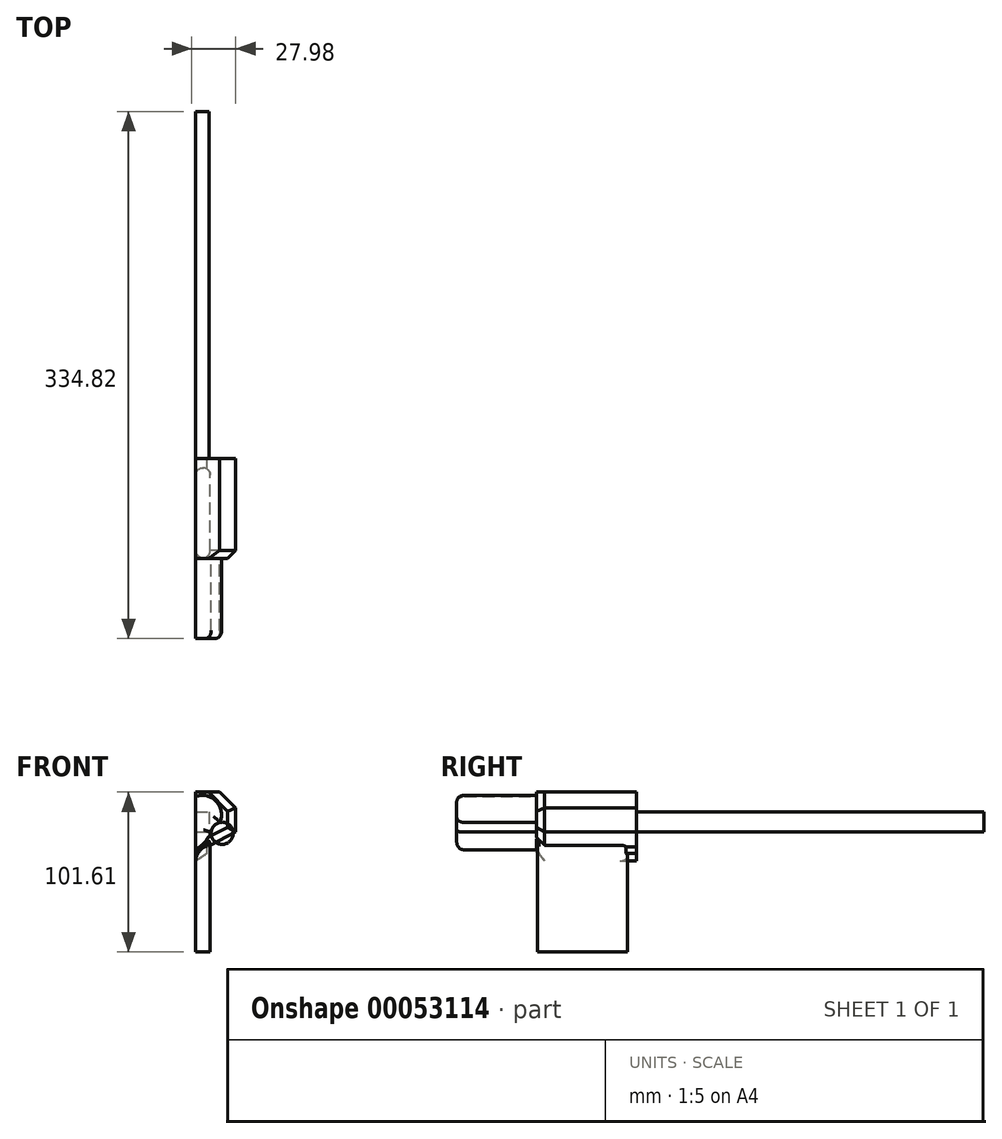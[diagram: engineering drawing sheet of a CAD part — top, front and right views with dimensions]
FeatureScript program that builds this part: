
annotation { "Feature Type Name" : "Feature", "Feature Type Description" : "" }
export const myFeature = defineFeature(function(context is Context, id is Id, definition is map)
    precondition{}
    {
        {
            var Q0;
            Q0=qCreatedBy(makeId("Top.planeOp"),FACE);
            var sketch = newSketch(context, id + "F0", { "sketchPlane" : qUnion([Q0])});
            skLineSegment(sketch, "E0.bottom", {"start": v(0, -78.27) * mm, "end": v(8.58, -78.27) * mm});
            skLineSegment(sketch, "E0.top", {"start": v(0, 142.25) * mm, "end": v(8.58, 142.25) * mm});
            skLineSegment(sketch, "E0.left", {"start": v(0, -78.27) * mm, "end": v(0, 142.25) * mm});
            skLineSegment(sketch, "E0.right", {"start": v(8.58, -78.27) * mm, "end": v(8.58, 142.25) * mm});
            skSolve(sketch);
        }
        {
            var Q0;
            Q0=makeQuery(id+"F0.imprint","IMPRINT",FACE,{"disambiguationData":[TD([[makeQuery(id+"F0.imprint","IMPRINT",EDGE,{"derivedFrom":sQuery(id+"F0.wireOp",EDGE,"E0.bottom")}),1.0]])]});
            extrude(context, id + "F1", {"entities" : qUnion([Q0]), "depth" : 12.7 * mm});
        }
        {
            var Q0;
            Q0=makeQuery(id+"F1.opExtrude","SWEPT_FACE",FACE,{"disambiguationData":[OSD([sQuery(id+"F0.wireOp",EDGE,"E0.bottom")])]});
            var sketch = newSketch(context, id + "F2", { "sketchPlane" : qUnion([Q0])});
            skLineSegment(sketch, "E1.bottom", {"start": v(0, 25.4) * mm, "end": v(25.38, 25.4) * mm});
            skLineSegment(sketch, "E1.left", {"start": v(0, 25.4) * mm, "end": v(0, 0) * mm});
            skLineSegment(sketch, "E1.right", {"start": v(25.38, 25.4) * mm, "end": v(25.38, 0) * mm});
            skLineSegment(sketch, "E2", {"start": v(25.38, 0) * mm, "end": v(7.29, -9.27) * mm});
            skLineSegment(sketch, "E3", {"start": v(7.29, -9.27) * mm, "end": v(7.29, -13.57) * mm});
            skLineSegment(sketch, "E4", {"start": v(7.29, -13.57) * mm, "end": v(0, -18.36) * mm});
            skLineSegment(sketch, "E5", {"start": v(0, -18.36) * mm, "end": v(0, 0) * mm});
            skSolve(sketch);
        }
        {
            var Q0;
            Q0 = qSketchRegion(id + "F2", true);
            extrude(context, id + "F3", {"entities" : qUnion([Q0]), "operationType" : NewBodyOperationType.ADD, "depth" : 63.5 * mm});
        }
        {
            var Q0;
            Q0=makeQuery(id+"F3.opExtrude","CAP_FACE",FACE,{"disambiguationData":[OSD([sQuery(id+"F2.wireOp",EDGE,"E1.bottom"),sQuery(id+"F2.wireOp",EDGE,"E1.left"),sQuery(id+"F2.wireOp",EDGE,"E1.right"),sQuery(id+"F2.wireOp",EDGE,"E2"),sQuery(id+"F2.wireOp",EDGE,"E3"),sQuery(id+"F2.wireOp",EDGE,"E4"),sQuery(id+"F2.wireOp",EDGE,"E5")])],"isStart":false});
            var sketch = newSketch(context, id + "F4", { "sketchPlane" : qUnion([Q0])});
            skArc(sketch, "E6", {"start": v(0, -11.2) * mm, "mid": v(5.78, -6.38) * mm, "end": v(9.78, 0) * mm});
            skArc(sketch, "E7", {"start": v(15.24, 6.16) * mm, "mid": v(11.51, 3.96) * mm, "end": v(9.78, 0) * mm});
            skArc(sketch, "E8", {"start": v(15.24, 6.16) * mm, "mid": v(13.13, 19.49) * mm, "end": v(0, 22.57) * mm});
            skLineSegment(sketch, "E9", {"start": v(0, 22.57) * mm, "end": v(0, -11.2) * mm});
            skSolve(sketch);
        }
        {
            var Q0;
            Q0 = qSketchRegion(id + "F4", true);
            extrude(context, id + "F5", {"entities" : qUnion([Q0]), "operationType" : NewBodyOperationType.ADD, "depth" : 50.8 * mm});
        }
        {
            var Q0;
            Q0=makeQuery(id+"F5.opExtrude","CAP_EDGE",EDGE,{"disambiguationData":[OSD([sQuery(id+"F4.wireOp",EDGE,"E8")])],"isStart":false});
            var Q1;
            Q1=makeQuery(id+"F5.opExtrude","CAP_EDGE",EDGE,{"disambiguationData":[OSD([sQuery(id+"F4.wireOp",EDGE,"E7")])],"isStart":false});
            var Q2;
            Q2=makeQuery(id+"F5.opExtrude","CAP_EDGE",EDGE,{"disambiguationData":[OSD([sQuery(id+"F4.wireOp",EDGE,"E6")])],"isStart":false});
            fillet(context, id + "F6", {"entities" : qUnion([Q0, Q1, Q2]), "radius" : 5.08 * mm, "tangentPropagation" : true, "rho" : .5, "crossSection" : FilletCrossSection.CONIC, "allowEdgeOverflow" : false});
        }
        {
            var Q0;
            Q0=makeQuery(id+"F3.opExtrude","SWEPT_EDGE",EDGE,{"disambiguationData":[OSD([sQuery(id+"F2.wireOp",EDGE,"E1.bottom"),sQuery(id+"F2.wireOp",EDGE,"E1.right")])]});
            chamfer(context, id + "F7", {"entities" : qUnion([Q0]), "width" : 10.16 * mm, "tangentPropagation" : true});
        }
        {
            var Q0;
            Q0=makeQuery(id+"F3.opExtrude","CAP_EDGE",EDGE,{"disambiguationData":[OSD([sQuery(id+"F2.wireOp",EDGE,"E1.right")])],"isStart":false});
            var Q1;
            {var subQ0=sQuery(id+"F2.wireOp",EDGE,"E1.right");var subQ1=sQuery(id+"F2.wireOp",EDGE,"E1.bottom");Q1=makeQuery(id+"F7.opChamfer","BLEND_EDGE",EDGE,{"blendedFrom":[makeQuery(id+"F3.opExtrude","SWEPT_EDGE",EDGE,{"disambiguationData":[OSD([subQ1,subQ0])]}),makeQuery(id+"F3.opExtrude","CAP_FACE",FACE,{"disambiguationData":[OSD([subQ1,sQuery(id+"F2.wireOp",EDGE,"E1.left"),subQ0,sQuery(id+"F2.wireOp",EDGE,"E2"),sQuery(id+"F2.wireOp",EDGE,"E3"),sQuery(id+"F2.wireOp",EDGE,"E4"),sQuery(id+"F2.wireOp",EDGE,"E5")])],"isStart":false})],"blendedInto":[makeQuery(id+"F3.opExtrude","CAP_FACE",FACE,{"disambiguationData":[OSD([subQ1,sQuery(id+"F2.wireOp",EDGE,"E1.left"),subQ0,sQuery(id+"F2.wireOp",EDGE,"E2"),sQuery(id+"F2.wireOp",EDGE,"E3"),sQuery(id+"F2.wireOp",EDGE,"E4"),sQuery(id+"F2.wireOp",EDGE,"E5")])],"isStart":false})]});}
            var Q2;
            Q2=makeQuery(id+"F3.opExtrude","CAP_EDGE",EDGE,{"disambiguationData":[OSD([sQuery(id+"F2.wireOp",EDGE,"E2")])],"isStart":false});
            chamfer(context, id + "F8", {"entities" : qUnion([Q0, Q1, Q2]), "width" : 5.08 * mm, "tangentPropagation" : true});
        }
        {
            var Q0;
            Q0=qCreatedBy(makeId("Top.planeOp"),FACE);
            var sketch = newSketch(context, id + "F9", { "sketchPlane" : qUnion([Q0])});
            skLineSegment(sketch, "E10.left", {"start": v(0, -88.68) * mm, "end": v(0, -136.65) * mm});
            skLineSegment(sketch, "E10.right", {"start": v(9.2, -88.68) * mm, "end": v(9.2, -136.65) * mm});
            skArc(sketch, "E11", {"start": v(9.2, -88.68) * mm, "mid": v(4.6, -84.08) * mm, "end": v(0, -88.68) * mm});
            skArc(sketch, "E12", {"start": v(0, -136.65) * mm, "mid": v(4.6, -141.25) * mm, "end": v(9.2, -136.65) * mm});
            skSolve(sketch);
        }
        {
            var Q0;
            Q0 = qSketchRegion(id + "F9", true);
            extrude(context, id + "F10", {"entities" : qUnion([Q0]), "operationType" : NewBodyOperationType.ADD, "oppositeDirection" : true, "depth" : 76.2 * mm});
        }
        {
            var Q0;
            Q0=makeQuery(id+"F3.opExtrude","CAP_EDGE",EDGE,{"disambiguationData":[OSD([sQuery(id+"F2.wireOp",EDGE,"E4")])],"isStart":false});
            chamfer(context, id + "F11", {"entities" : qUnion([Q0]), "width" : 5.08 * mm, "tangentPropagation" : true});
        }
    });
